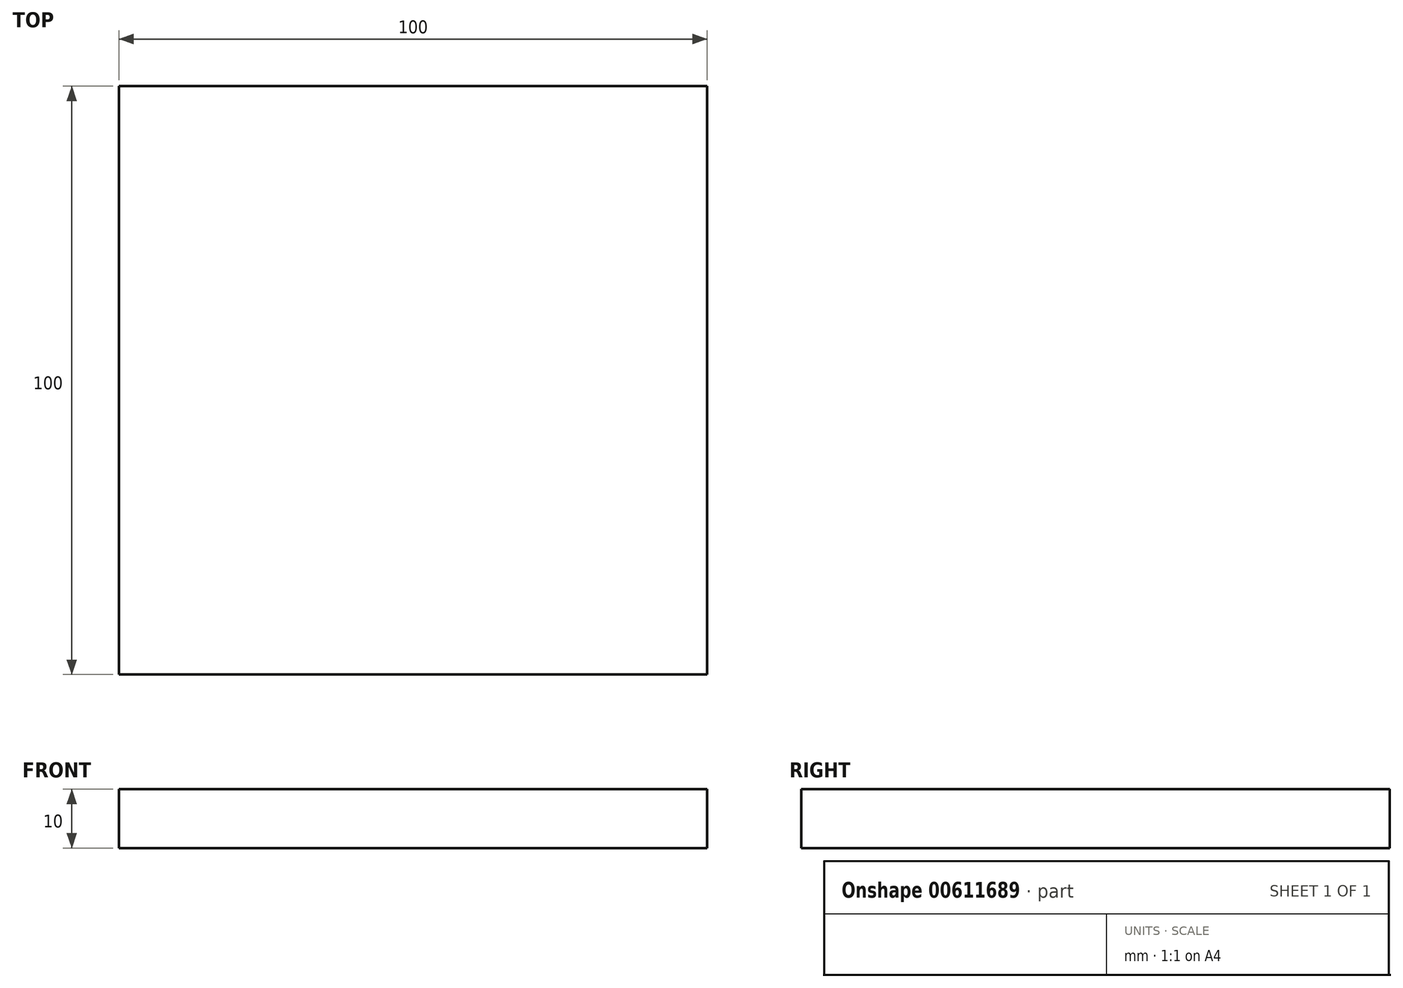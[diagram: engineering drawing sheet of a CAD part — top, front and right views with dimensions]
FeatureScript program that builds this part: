
annotation { "Feature Type Name" : "Feature", "Feature Type Description" : "" }
export const myFeature = defineFeature(function(context is Context, id is Id, definition is map)
    precondition{}
    {
        {
            var Q0;
            Q0=qCreatedBy(makeId("Top.planeOp"),FACE);
            var sketch = newSketch(context, id + "F0", { "sketchPlane" : qUnion([Q0])});
            skLineSegment(sketch, "E0.bottom", {"start": v(50, 50) * mm, "end": v(-50, 50) * mm});
            skLineSegment(sketch, "E0.top", {"start": v(50, -50) * mm, "end": v(-50, -50) * mm});
            skLineSegment(sketch, "E0.left", {"start": v(50, 50) * mm, "end": v(50, -50) * mm});
            skLineSegment(sketch, "E0.right", {"start": v(-50, 50) * mm, "end": v(-50, -50) * mm});
            skPoint(sketch, "E0.middle", {"position": v(0, 0) * mm});
            skSolve(sketch);
        }
        {
            var Q0;
            Q0=makeQuery(id+"F0.imprint","IMPRINT",FACE,{"disambiguationData":[TD([[makeQuery(id+"F0.imprint","IMPRINT",EDGE,{"derivedFrom":sQuery(id+"F0.wireOp",EDGE,"E0.bottom")}),1.0]])]});
            extrude(context, id + "F1", {"entities" : qUnion([Q0]), "depth" : 10 * mm, "offsetDistance" : 25 * mm});
        }
    });
